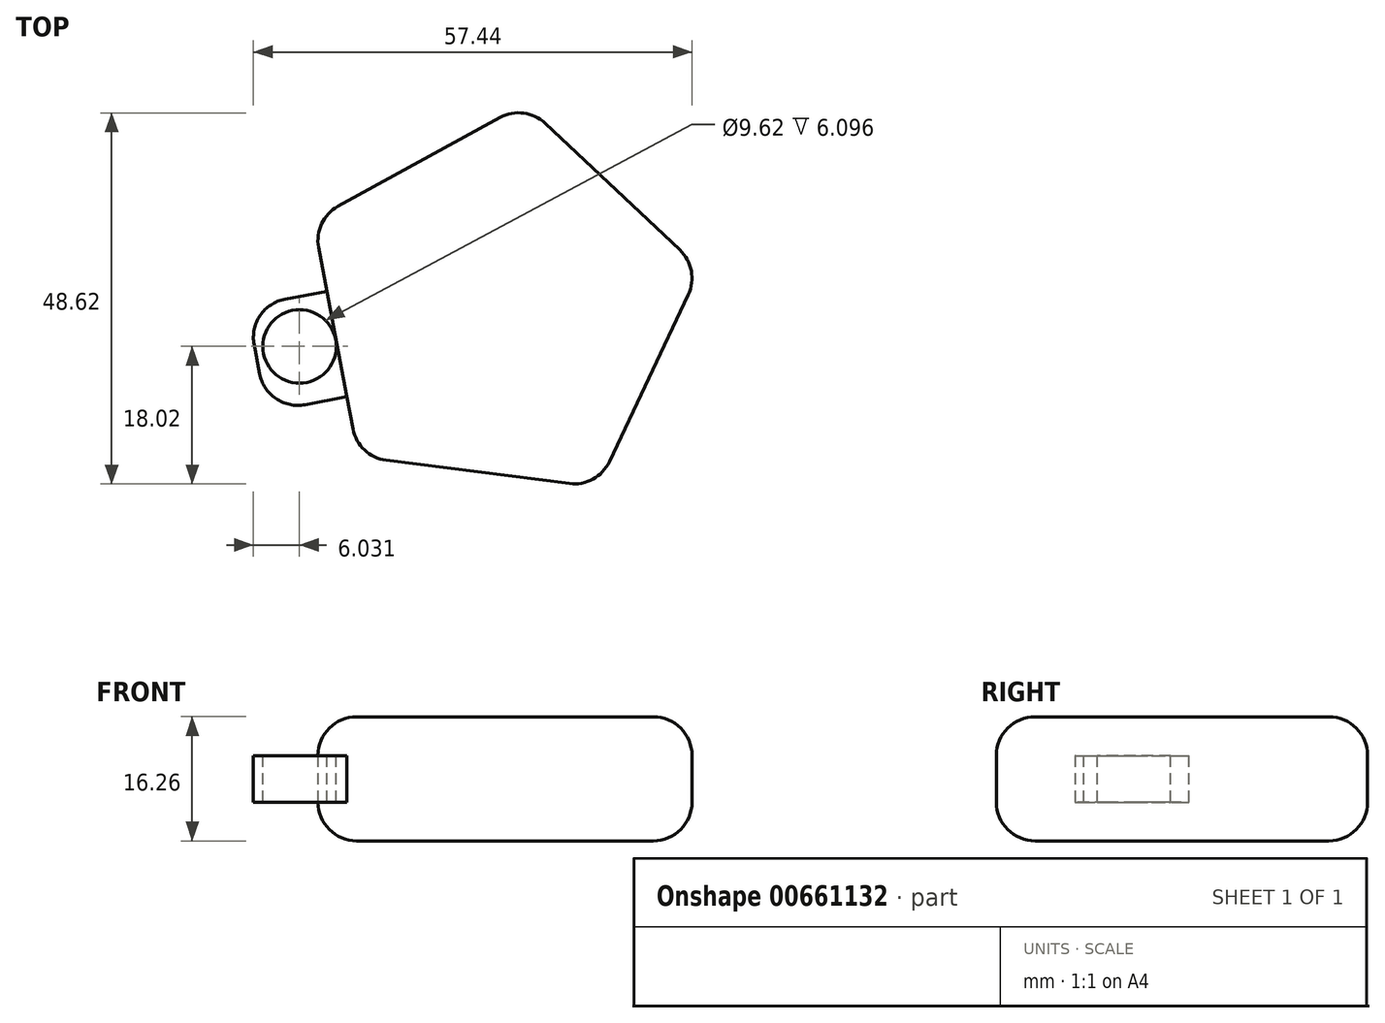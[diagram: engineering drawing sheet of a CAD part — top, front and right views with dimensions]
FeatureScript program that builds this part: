
annotation { "Feature Type Name" : "Feature", "Feature Type Description" : "" }
export const myFeature = defineFeature(function(context is Context, id is Id, definition is map)
    precondition{}
    {
        {
            var Q0;
            Q0=qCreatedBy(makeId("Top.planeOp"),FACE);
            var sketch = newSketch(context, id + "F0", { "sketchPlane" : qUnion([Q0])});
            skCircle(sketch, "E0.cCircle", {"center": v(0, 0) * mm, "radius": 21.73 * mm, "construction": true});
            skLineSegment(sketch, "E0.0", {"start": v(3.4, 26.64) * mm, "end": v(26.4, 5) * mm});
            skLineSegment(sketch, "E0.1", {"start": v(26.4, 5) * mm, "end": v(12.9, -23.55) * mm});
            skLineSegment(sketch, "E0.2", {"start": v(12.9, -23.55) * mm, "end": v(-18.41, -19.56) * mm});
            skLineSegment(sketch, "E0.3", {"start": v(-18.41, -19.56) * mm, "end": v(-24.29, 11.47) * mm});
            skLineSegment(sketch, "E0.4", {"start": v(-24.29, 11.47) * mm, "end": v(3.4, 26.64) * mm});
            skPoint(sketch, "E0.0.midPoint", {"position": v(14.9, 15.82) * mm});
            skSolve(sketch);
        }
        {
            var Q0;
            Q0 = qSketchRegion(id + "F0", true);
            extrude(context, id + "F1", {"entities" : qUnion([Q0]), "depth" : 16.26 * mm, "offsetDistance" : 25.4 * mm});
        }
        {
            var Q0;
            Q0=makeQuery(id+"F1.opExtrude","SWEPT_EDGE",EDGE,{"disambiguationData":[OSD([sQuery(id+"F0.wireOp",EDGE,"E0.2"),sQuery(id+"F0.wireOp",EDGE,"E0.3")])]});
            var Q1;
            Q1=makeQuery(id+"F1.opExtrude","CAP_EDGE",EDGE,{"disambiguationData":[OSD([sQuery(id+"F0.wireOp",EDGE,"E0.2")])],"isStart":true});
            var Q2;
            Q2=makeQuery(id+"F1.opExtrude","CAP_EDGE",EDGE,{"disambiguationData":[OSD([sQuery(id+"F0.wireOp",EDGE,"E0.2")])],"isStart":false});
            var Q3;
            Q3=makeQuery(id+"F1.opExtrude","CAP_EDGE",EDGE,{"disambiguationData":[OSD([sQuery(id+"F0.wireOp",EDGE,"E0.3")])],"isStart":true});
            var Q4;
            Q4=makeQuery(id+"F1.opExtrude","CAP_EDGE",EDGE,{"disambiguationData":[OSD([sQuery(id+"F0.wireOp",EDGE,"E0.4")])],"isStart":true});
            var Q5;
            Q5=makeQuery(id+"F1.opExtrude","CAP_EDGE",EDGE,{"disambiguationData":[OSD([sQuery(id+"F0.wireOp",EDGE,"E0.0")])],"isStart":true});
            var Q6;
            Q6=makeQuery(id+"F1.opExtrude","CAP_EDGE",EDGE,{"disambiguationData":[OSD([sQuery(id+"F0.wireOp",EDGE,"E0.1")])],"isStart":true});
            var Q7;
            Q7=makeQuery(id+"F1.opExtrude","CAP_EDGE",EDGE,{"disambiguationData":[OSD([sQuery(id+"F0.wireOp",EDGE,"E0.1")])],"isStart":false});
            var Q8;
            Q8=makeQuery(id+"F1.opExtrude","CAP_EDGE",EDGE,{"disambiguationData":[OSD([sQuery(id+"F0.wireOp",EDGE,"E0.0")])],"isStart":false});
            var Q9;
            Q9=makeQuery(id+"F1.opExtrude","CAP_EDGE",EDGE,{"disambiguationData":[OSD([sQuery(id+"F0.wireOp",EDGE,"E0.4")])],"isStart":false});
            var Q10;
            Q10=makeQuery(id+"F1.opExtrude","CAP_EDGE",EDGE,{"disambiguationData":[OSD([sQuery(id+"F0.wireOp",EDGE,"E0.3")])],"isStart":false});
            var Q11;
            Q11=makeQuery(id+"F1.opExtrude","SWEPT_EDGE",EDGE,{"disambiguationData":[OSD([sQuery(id+"F0.wireOp",EDGE,"E0.0"),sQuery(id+"F0.wireOp",EDGE,"E0.4")])]});
            var Q12;
            Q12=makeQuery(id+"F1.opExtrude","SWEPT_EDGE",EDGE,{"disambiguationData":[OSD([sQuery(id+"F0.wireOp",EDGE,"E0.3"),sQuery(id+"F0.wireOp",EDGE,"E0.4")])]});
            var Q13;
            Q13=makeQuery(id+"F1.opExtrude","SWEPT_EDGE",EDGE,{"disambiguationData":[OSD([sQuery(id+"F0.wireOp",EDGE,"E0.1"),sQuery(id+"F0.wireOp",EDGE,"E0.2")])]});
            var Q14;
            Q14=makeQuery(id+"F1.opExtrude","SWEPT_FACE",FACE,{"disambiguationData":[OSD([sQuery(id+"F0.wireOp",EDGE,"E0.0")])]});
            fillet(context, id + "F2", {"entities" : qUnion([Q0, Q1, Q2, Q3, Q4, Q5, Q6, Q7, Q8, Q9, Q10, Q11, Q12, Q13, Q14]), "radius" : 5.08 * mm, "tangentPropagation" : true, "allowEdgeOverflow" : false});
        }
        {
            var Q0;
            Q0=makeQuery(id+"F1.opExtrude","SWEPT_FACE",FACE,{"disambiguationData":[OSD([sQuery(id+"F0.wireOp",EDGE,"E0.3")])]});
            var sketch = newSketch(context, id + "F3", { "sketchPlane" : qUnion([Q0])});
            skLineSegment(sketch, "E1.bottom", {"start": v(7.8, 5.08) * mm, "end": v(-6.27, 5.08) * mm});
            skLineSegment(sketch, "E1.top", {"start": v(7.8, 11.18) * mm, "end": v(-6.27, 11.18) * mm});
            skLineSegment(sketch, "E1.left", {"start": v(7.8, 5.08) * mm, "end": v(7.8, 11.18) * mm});
            skLineSegment(sketch, "E1.right", {"start": v(-6.27, 5.08) * mm, "end": v(-6.27, 11.18) * mm});
            skSolve(sketch);
        }
        {
            var Q0;
            Q0=makeQuery(id+"F3.imprint","IMPRINT",FACE,{"disambiguationData":[TD([[makeQuery(id+"F3.imprint","IMPRINT",EDGE,{"derivedFrom":sQuery(id+"F3.wireOp",EDGE,"E1.bottom")}),1.0]])]});
            extrude(context, id + "F4", {"entities" : qUnion([Q0]), "operationType" : NewBodyOperationType.ADD, "depth" : 10.67 * mm, "offsetDistance" : 25.4 * mm});
        }
        {
            var Q0;
            Q0=makeQuery(id+"F4.opExtrude","CAP_EDGE",EDGE,{"disambiguationData":[OSD([sQuery(id+"F3.wireOp",EDGE,"E1.left")])],"isStart":false});
            var Q1;
            Q1=makeQuery(id+"F4.opExtrude","CAP_EDGE",EDGE,{"disambiguationData":[OSD([sQuery(id+"F3.wireOp",EDGE,"E1.right")])],"isStart":false});
            fillet(context, id + "F5", {"entities" : qUnion([Q0, Q1]), "radius" : 5.08 * mm, "tangentPropagation" : true, "allowEdgeOverflow" : false});
        }
        {
            var Q0;
            Q0=makeQuery(id+"F4.opExtrude","SWEPT_FACE",FACE,{"disambiguationData":[OSD([sQuery(id+"F3.wireOp",EDGE,"E1.top")])]});
            var sketch = newSketch(context, id + "F6", { "sketchPlane" : qUnion([Q0])});
            skCircle(sketch, "E2", {"center": v(-26.1, -5.11) * mm, "radius": 4.81 * mm});
            skSolve(sketch);
        }
        {
            var Q0;
            Q0=makeQuery(id+"F6.imprint","IMPRINT",FACE,{"disambiguationData":[TD([[makeQuery(id+"F6.imprint","IMPRINT",EDGE,{"derivedFrom":sQuery(id+"F6.wireOp",EDGE,"E2")}),1.0]])]});
            extrude(context, id + "F7", {"entities" : qUnion([Q0]), "operationType" : NewBodyOperationType.REMOVE, "oppositeDirection" : true, "depth" : 25.4 * mm, "offsetDistance" : 25.4 * mm});
        }
    });
